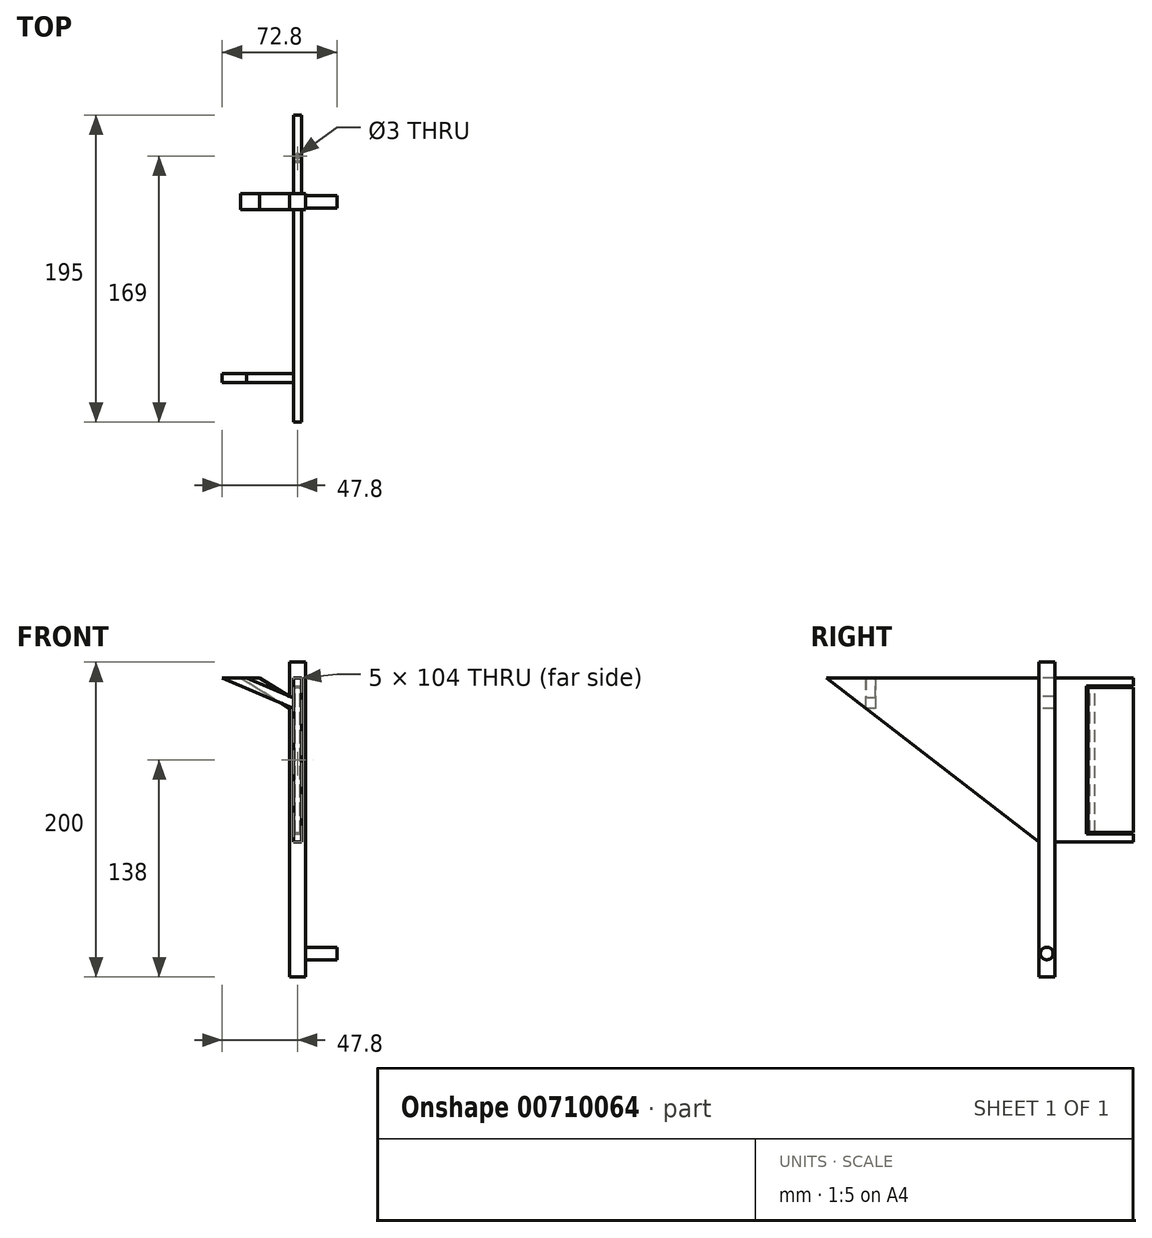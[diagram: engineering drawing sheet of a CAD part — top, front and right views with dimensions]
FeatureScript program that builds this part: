
annotation { "Feature Type Name" : "Feature", "Feature Type Description" : "" }
export const myFeature = defineFeature(function(context is Context, id is Id, definition is map)
    precondition{}
    {
        {
            var Q0;
            Q0=qCreatedBy(makeId("Front.planeOp"),FACE);
            var sketch = newSketch(context, id + "F0", { "sketchPlane" : qUnion([Q0])});
            skLineSegment(sketch, "E0.bottom", {"start": v(5, -100) * mm, "end": v(-5, -100) * mm});
            skLineSegment(sketch, "E0.top", {"start": v(5, 100) * mm, "end": v(-5, 100) * mm});
            skLineSegment(sketch, "E0.left", {"start": v(5, -100) * mm, "end": v(5, 100) * mm});
            skLineSegment(sketch, "E0.right", {"start": v(-5, -100) * mm, "end": v(-5, 100) * mm});
            skPoint(sketch, "E0.middle", {"position": v(0, 0) * mm});
            skSolve(sketch);
        }
        {
            var Q0;
            Q0 = qSketchRegion(id + "F0", true);
            extrude(context, id + "F1", {"entities" : qUnion([Q0]), "depth" : 10 * mm, "offsetDistance" : 25 * mm});
        }
        {
            var Q0;
            Q0=makeQuery(id+"F1.opExtrude","CAP_FACE",FACE,{"disambiguationData":[OSD([sQuery(id+"F0.wireOp",EDGE,"E0.bottom"),sQuery(id+"F0.wireOp",EDGE,"E0.top"),sQuery(id+"F0.wireOp",EDGE,"E0.left"),sQuery(id+"F0.wireOp",EDGE,"E0.right")])],"isStart":false});
            var sketch = newSketch(context, id + "F2", { "sketchPlane" : qUnion([Q0])});
            skLineSegment(sketch, "E1", {"start": v(0, 90) * mm, "end": v(2.5, 90) * mm});
            skLineSegment(sketch, "E2", {"start": v(2.5, 90) * mm, "end": v(2.5, -14) * mm});
            skLineSegment(sketch, "E3", {"start": v(2.5, -14) * mm, "end": v(0, -14) * mm});
            skLineSegment(sketch, "E4", {"start": v(0, -14) * mm, "end": v(-2.5, -14) * mm});
            skLineSegment(sketch, "E5", {"start": v(-2.5, -14) * mm, "end": v(-2.5, 90) * mm});
            skLineSegment(sketch, "E6", {"start": v(-2.5, 90) * mm, "end": v(0, 90) * mm});
            skSolve(sketch);
        }
        {
            var Q0;
            Q0 = qSketchRegion(id + "F2", true);
            extrude(context, id + "F3", {"entities" : qUnion([Q0]), "operationType" : NewBodyOperationType.ADD, "depth" : 135 * mm, "offsetDistance" : 25 * mm});
        }
        {
            var Q0;
            Q0=makeQuery(id+"F3.opExtrude","SWEPT_FACE",FACE,{"disambiguationData":[OSD([sQuery(id+"F2.wireOp",EDGE,"E2")])]});
            var sketch = newSketch(context, id + "F4", { "sketchPlane" : qUnion([Q0])});
            skLineSegment(sketch, "E7", {"start": v(-145, 90) * mm, "end": v(-145, -14) * mm});
            skLineSegment(sketch, "E8", {"start": v(-145, -14) * mm, "end": v(-10, -14) * mm});
            skLineSegment(sketch, "E9", {"start": v(-10, -14) * mm, "end": v(-145, 90) * mm});
            skSolve(sketch);
        }
        {
            var Q0;
            Q0 = qSketchRegion(id + "F4", true);
            extrude(context, id + "F5", {"entities" : qUnion([Q0]), "operationType" : NewBodyOperationType.REMOVE, "endBound" : BoundingType.THROUGH_ALL, "oppositeDirection" : true, "depth" : 25 * mm, "offsetDistance" : 25 * mm});
        }
        {
            var Q0;
            Q0=makeQuery(id+"F3.opExtrude","SWEPT_FACE",FACE,{"disambiguationData":[OSD([sQuery(id+"F2.wireOp",EDGE,"E5")])]});
            var sketch = newSketch(context, id + "F6", { "sketchPlane" : qUnion([Q0])});
            skLineSegment(sketch, "E10", {"start": v(10, 90) * mm, "end": v(114, 90) * mm});
            skLineSegment(sketch, "E11", {"start": v(114, 90) * mm, "end": v(120, 90) * mm});
            skLineSegment(sketch, "E12", {"start": v(114, 90) * mm, "end": v(114, 84) * mm});
            skLineSegment(sketch, "E13", {"start": v(114, 84) * mm, "end": v(120, 84) * mm});
            skLineSegment(sketch, "E14", {"start": v(120, 84) * mm, "end": v(120, 90) * mm});
            skLineSegment(sketch, "E15", {"start": v(10, 90) * mm, "end": v(10, 70.74) * mm});
            skLineSegment(sketch, "E16", {"start": v(10, 70.74) * mm, "end": v(114, 70.74) * mm});
            skLineSegment(sketch, "E17", {"start": v(114, 70.74) * mm, "end": v(120, 70.74) * mm});
            skLineSegment(sketch, "E18", {"start": v(114, 70.74) * mm, "end": v(114, 76.74) * mm});
            skLineSegment(sketch, "E19", {"start": v(114, 76.74) * mm, "end": v(120, 76.74) * mm});
            skLineSegment(sketch, "E20", {"start": v(120, 76.74) * mm, "end": v(120, 70.74) * mm});
            skLineSegment(sketch, "E21", {"start": v(120, 90) * mm, "end": v(120, 70.74) * mm});
            skLineSegment(sketch, "E22", {"start": v(114, 76.74) * mm, "end": v(114, 84) * mm});
            skLineSegment(sketch, "E23.bottom", {"start": v(120, 90) * mm, "end": v(114, 90) * mm});
            skLineSegment(sketch, "E23.top", {"start": v(120, 92) * mm, "end": v(114, 92) * mm});
            skLineSegment(sketch, "E23.left", {"start": v(120, 90) * mm, "end": v(120, 92) * mm});
            skLineSegment(sketch, "E23.right", {"start": v(114, 90) * mm, "end": v(114, 92) * mm});
            skSolve(sketch);
        }
        {
            var Q0;
            {var subQ0=sQuery(id+"F6.wireOp",EDGE,"E11");Q0=makeQuery(id+"F6.imprint","IMPRINT",FACE,{"disambiguationData":[TD([[makeQuery(id+"F6.imprint","IMPRINT",EDGE,{"derivedFrom":subQ0}),1.0]])]});}
            var Q1;
            {var subQ0=sQuery(id+"F6.wireOp",EDGE,"E17");Q1=makeQuery(id+"F6.imprint","IMPRINT",FACE,{"disambiguationData":[TD([[makeQuery(id+"F6.imprint","IMPRINT",EDGE,{"derivedFrom":subQ0}),1.0]])]});}
            var Q2;
            {var subQ0=sQuery(id+"F6.wireOp",EDGE,"E13");Q2=makeQuery(id+"F6.imprint","IMPRINT",FACE,{"disambiguationData":[TD([[makeQuery(id+"F6.imprint","IMPRINT",EDGE,{"derivedFrom":subQ0}),-1.0]])]});}
            var Q3;
            Q3=makeQuery(id+"F6.imprint","IMPRINT",FACE,{"disambiguationData":[TD([[makeQuery(id+"F6.imprint","IMPRINT",EDGE,{"derivedFrom":sQuery(id+"F6.wireOp",EDGE,"E12")}),1.0]])]});
            var Q4;
            Q4=makeQuery(id+"F6.imprint","IMPRINT",FACE,{"disambiguationData":[TD([[makeQuery(id+"F6.imprint","IMPRINT",EDGE,{"derivedFrom":sQuery(id+"F6.wireOp",EDGE,"E23.bottom")}),-1.0]])]});
            extrude(context, id + "F7", {"entities" : qUnion([Q0, Q1, Q2, Q3, Q4]), "operationType" : NewBodyOperationType.ADD, "depth" : 50 * mm, "offsetDistance" : 25 * mm});
        }
        {
            var Q0;
            Q0=makeQuery(id+"F7.opExtrude","SWEPT_FACE",FACE,{"disambiguationData":[OSD([sQuery(id+"F6.wireOp",EDGE,"E21")])]});
            var sketch = newSketch(context, id + "F8", { "sketchPlane" : qUnion([Q0])});
            skLineSegment(sketch, "E24", {"start": v(-2.5, 70.74) * mm, "end": v(-52.5, 92) * mm});
            skLineSegment(sketch, "E25", {"start": v(-37.17, 92) * mm, "end": v(-2.5, 77.26) * mm});
            skSolve(sketch);
        }
        {
            var Q0;
            Q0=makeQuery(id+"F8.imprint","IMPRINT",FACE,{"disambiguationData":[TD([[makeQuery(id+"F8.imprint","IMPRINT",EDGE,{"derivedFrom":sQuery(id+"F8.wireOp",EDGE,"qwdXAB4e-E5ou-LqlY-9mqs-tjVmSu6iFq8c")}),1.0]])]});
            var Q1;
            {var subQ0=sQuery(id+"F8.wireOp",EDGE,"3mmgTVSa-EUJ8-fqU7-aLnw-NF2mhHhyj2O0");Q1=makeQuery(id+"F8.imprint","IMPRINT",FACE,{"disambiguationData":[TD([[makeQuery(id+"F8.imprint","IMPRINT",EDGE,{"derivedFrom":subQ0}),1.0]])]});}
            var Q2;
            {var subQ0=sQuery(id+"F8.wireOp",EDGE,"P0UW7KZ7-9kCL-0TL6-S78o-fbrZpAh6waou");Q2=makeQuery(id+"F8.imprint","IMPRINT",FACE,{"disambiguationData":[TD([[makeQuery(id+"F8.imprint","IMPRINT",EDGE,{"derivedFrom":subQ0}),1.0]])]});}
            var Q3;
            Q3=makeQuery(id+"F8.imprint","IMPRINT",FACE,{"disambiguationData":[TD([[makeQuery(id+"F8.imprint","IMPRINT",EDGE,{"derivedFrom":sQuery(id+"F8.wireOp",EDGE,"kPvC1WPp-rgsQ-izWo-Zl4w-EBVaQ9JV2pb9")}),1.0]])]});
            var Q4;
            Q4=makeQuery(id+"F8.imprint","IMPRINT",FACE,{"disambiguationData":[TD([[makeQuery(id+"F8.imprint","IMPRINT",EDGE,{"derivedFrom":sQuery(id+"F8.wireOp",EDGE,"E24")}),1.0]])]});
            var Q5;
            {var subQ0=sQuery(id+"F8.wireOp",EDGE,"E25");Q5=makeQuery(id+"F8.imprint","IMPRINT",FACE,{"disambiguationData":[TD([[makeQuery(id+"F8.imprint","IMPRINT",EDGE,{"derivedFrom":subQ0}),1.0]])]});}
            var Q6;
            Q6=makeQuery(id+"F7.opExtrude","SWEPT_FACE",FACE,{"disambiguationData":[OSD([sQuery(id+"F6.wireOp",EDGE,"E12"),sQuery(id+"F6.wireOp",EDGE,"E18"),sQuery(id+"F6.wireOp",EDGE,"E22")])]});
            extrude(context, id + "F9", {"entities" : qUnion([Q0, Q1, Q2, Q3, Q4, Q5]), "operationType" : NewBodyOperationType.REMOVE, "endBound" : BoundingType.UP_TO_SURFACE, "oppositeDirection" : true, "depth" : 25 * mm, "endBoundEntityFace" : qUnion([Q6]), "offsetDistance" : 25 * mm});
        }
        {
            var Q0;
            Q0=makeQuery(id+"F1.opExtrude","SWEPT_FACE",FACE,{"disambiguationData":[OSD([sQuery(id+"F0.wireOp",EDGE,"E0.right")])]});
            var sketch = newSketch(context, id + "F10", { "sketchPlane" : qUnion([Q0])});
            skLineSegment(sketch, "E26", {"start": v(5, 100) * mm, "end": v(5, 45.97) * mm});
            skLineSegment(sketch, "E27", {"start": v(5, 100) * mm, "end": v(5, 90) * mm});
            skLineSegment(sketch, "E28", {"start": v(5, 90) * mm, "end": v(5, 70.75) * mm});
            skLineSegment(sketch, "E29", {"start": v(5, 70.75) * mm, "end": v(10, 70.75) * mm});
            skLineSegment(sketch, "E30", {"start": v(10, 70.75) * mm, "end": v(10, 80.75) * mm});
            skLineSegment(sketch, "E31", {"start": v(10, 80.75) * mm, "end": v(0, 80.75) * mm});
            skLineSegment(sketch, "E32", {"start": v(0, 80.75) * mm, "end": v(0, 70.75) * mm});
            skLineSegment(sketch, "E33", {"start": v(0, 70.75) * mm, "end": v(5, 70.75) * mm});
            skLineSegment(sketch, "E34", {"start": v(10, 80.75) * mm, "end": v(10, 90) * mm});
            skLineSegment(sketch, "E35", {"start": v(10, 90) * mm, "end": v(0, 90) * mm});
            skLineSegment(sketch, "E36", {"start": v(0, 90) * mm, "end": v(0, 80.75) * mm});
            skSolve(sketch);
        }
        {
            var Q0;
            {var subQ0=sQuery(id+"F10.wireOp",EDGE,"E29");Q0=makeQuery(id+"F10.imprint","IMPRINT",FACE,{"disambiguationData":[TD([[makeQuery(id+"F10.imprint","IMPRINT",EDGE,{"derivedFrom":subQ0}),1.0]])]});}
            var Q1;
            {var subQ4=sQuery(id+"F10.wireOp",EDGE,"E32");Q1=makeQuery(id+"F10.imprint","IMPRINT",FACE,{"disambiguationData":[TD([[makeQuery(id+"F10.imprint","IMPRINT",EDGE,{"derivedFrom":subQ4}),-1.0]])]});}
            var Q2;
            {var subQ5=sQuery(id+"F10.wireOp",EDGE,"E36");Q2=makeQuery(id+"F10.imprint","IMPRINT",FACE,{"disambiguationData":[TD([[makeQuery(id+"F10.imprint","IMPRINT",EDGE,{"derivedFrom":subQ5}),-1.0]])]});}
            var Q3;
            {var subQ5=sQuery(id+"F10.wireOp",EDGE,"E34");Q3=makeQuery(id+"F10.imprint","IMPRINT",FACE,{"disambiguationData":[TD([[makeQuery(id+"F10.imprint","IMPRINT",EDGE,{"derivedFrom":subQ5}),1.0]])]});}
            var Q4;
            {var subQ0=sQuery(id+"F10.wireOp",EDGE,"E27");Q4=makeQuery(id+"F10.imprint","IMPRINT",FACE,{"disambiguationData":[TD([[makeQuery(id+"F10.imprint","IMPRINT",EDGE,{"derivedFrom":subQ0}),1.0]])]});}
            var Q5;
            {var subQ0=sQuery(id+"F10.wireOp",EDGE,"E27");Q5=makeQuery(id+"F10.imprint","IMPRINT",FACE,{"disambiguationData":[TD([[makeQuery(id+"F10.imprint","IMPRINT",EDGE,{"derivedFrom":subQ0}),-1.0]])]});}
            extrude(context, id + "F11", {"entities" : qUnion([Q0, Q1, Q2, Q3, Q4, Q5]), "operationType" : NewBodyOperationType.ADD, "depth" : 47.5 * mm, "offsetDistance" : 25 * mm});
        }
        {
            var Q0;
            Q0=makeQuery(id+"F11.boolean.opBoolean","MERGE",FACE,{"derivedFrom":[makeQuery(id+"F1.opExtrude","CAP_FACE",FACE,{"disambiguationData":[OSD([sQuery(id+"F0.wireOp",EDGE,"E0.bottom"),sQuery(id+"F0.wireOp",EDGE,"E0.top"),sQuery(id+"F0.wireOp",EDGE,"E0.left"),sQuery(id+"F0.wireOp",EDGE,"E0.right")])],"isStart":false}),makeQuery(id+"F11.opExtrude","SWEPT_FACE",FACE,{"disambiguationData":[OSD([sQuery(id+"F10.wireOp",EDGE,"E30"),sQuery(id+"F10.wireOp",EDGE,"E34")])]})]});
            var sketch = newSketch(context, id + "F12", { "sketchPlane" : qUnion([Q0])});
            skLineSegment(sketch, "E37", {"start": v(-52.5, 100) * mm, "end": v(-5, 70.75) * mm});
            skLineSegment(sketch, "E38", {"start": v(-5, 70.75) * mm, "end": v(-2.5, 70.75) * mm});
            skLineSegment(sketch, "E39", {"start": v(-5, 70.75) * mm, "end": v(-5, 100) * mm});
            skLineSegment(sketch, "E40", {"start": v(-40.23, 100) * mm, "end": v(-5, 78.3) * mm});
            skSolve(sketch);
        }
        {
            var Q0;
            {var subQ6=sQuery(id+"F12.wireOp",EDGE,"LR92XTVL-ZGK5-bEUs-Z0Es-jbydp57ibUwi");Q0=makeQuery(id+"F12.imprint","IMPRINT",FACE,{"disambiguationData":[TD([[makeQuery(id+"F12.imprint","IMPRINT",EDGE,{"derivedFrom":subQ6}),-1.0]])]});}
            var Q1;
            Q1=makeQuery(id+"F12.imprint","IMPRINT",FACE,{"disambiguationData":[TD([[makeQuery(id+"F12.imprint","IMPRINT",EDGE,{"derivedFrom":sQuery(id+"F12.wireOp",EDGE,"E37")}),-1.0]])]});
            var Q2;
            {var subQ5=sQuery(id+"F12.wireOp",EDGE,"E40");Q2=makeQuery(id+"F12.imprint","IMPRINT",FACE,{"disambiguationData":[TD([[makeQuery(id+"F12.imprint","IMPRINT",EDGE,{"derivedFrom":subQ5}),1.0]])]});}
            var Q3;
            Q3=makeQuery(id+"F11.boolean.opBoolean","MERGE",FACE,{"derivedFrom":[makeQuery(id+"F1.opExtrude","CAP_FACE",FACE,{"disambiguationData":[OSD([sQuery(id+"F0.wireOp",EDGE,"E0.bottom"),sQuery(id+"F0.wireOp",EDGE,"E0.top"),sQuery(id+"F0.wireOp",EDGE,"E0.left"),sQuery(id+"F0.wireOp",EDGE,"E0.right")])],"isStart":true}),makeQuery(id+"F11.opExtrude","SWEPT_FACE",FACE,{"disambiguationData":[OSD([sQuery(id+"F10.wireOp",EDGE,"E32"),sQuery(id+"F10.wireOp",EDGE,"E36")])]})]});
            extrude(context, id + "F13", {"entities" : qUnion([Q0, Q1, Q2]), "operationType" : NewBodyOperationType.REMOVE, "endBound" : BoundingType.UP_TO_SURFACE, "oppositeDirection" : true, "depth" : 25 * mm, "endBoundEntityFace" : qUnion([Q3]), "offsetDistance" : 25 * mm});
        }
        {
            var Q0;
            Q0=makeQuery(id+"F1.opExtrude","SWEPT_FACE",FACE,{"disambiguationData":[OSD([sQuery(id+"F0.wireOp",EDGE,"E0.left")])]});
            var sketch = newSketch(context, id + "F14", { "sketchPlane" : qUnion([Q0])});
            skLineSegment(sketch, "E41", {"start": v(-5, -100) * mm, "end": v(-5, -85) * mm});
            skCircle(sketch, "E42", {"center": v(-5, -85) * mm, "radius": 4 * mm});
            skSolve(sketch);
        }
        {
            var Q0;
            Q0=makeQuery(id+"F14.imprint","IMPRINT",FACE,{"disambiguationData":[TD([[makeQuery(id+"F14.imprint","IMPRINT",EDGE,{"derivedFrom":sQuery(id+"F14.wireOp",EDGE,"E42")}),1.0]])]});
            extrude(context, id + "F15", {"entities" : qUnion([Q0]), "operationType" : NewBodyOperationType.ADD, "depth" : 20 * mm, "offsetDistance" : 25 * mm});
        }
        {
            var Q0;
            Q0=makeQuery(id+"F11.boolean.opBoolean","MERGE",FACE,{"derivedFrom":[makeQuery(id+"F1.opExtrude","CAP_FACE",FACE,{"disambiguationData":[OSD([sQuery(id+"F0.wireOp",EDGE,"E0.bottom"),sQuery(id+"F0.wireOp",EDGE,"E0.top"),sQuery(id+"F0.wireOp",EDGE,"E0.left"),sQuery(id+"F0.wireOp",EDGE,"E0.right")])],"isStart":true}),makeQuery(id+"F11.opExtrude","SWEPT_FACE",FACE,{"disambiguationData":[OSD([sQuery(id+"F10.wireOp",EDGE,"E32"),sQuery(id+"F10.wireOp",EDGE,"E36")])]})]});
            var sketch = newSketch(context, id + "F16", { "sketchPlane" : qUnion([Q0])});
            skLineSegment(sketch, "E43", {"start": v(0, 90) * mm, "end": v(2.5, 90) * mm});
            skLineSegment(sketch, "E44", {"start": v(0, 90) * mm, "end": v(-2.5, 90) * mm});
            skLineSegment(sketch, "E45.bottom", {"start": v(-2.5, 90) * mm, "end": v(2.5, 90) * mm});
            skLineSegment(sketch, "E45.top", {"start": v(-2.5, -14) * mm, "end": v(2.5, -14) * mm});
            skLineSegment(sketch, "E45.left", {"start": v(-2.5, 90) * mm, "end": v(-2.5, -14) * mm});
            skLineSegment(sketch, "E45.right", {"start": v(2.5, 90) * mm, "end": v(2.5, -14) * mm});
            skPoint(sketch, "E46.start.orphan", {"position": v(0, 100) * mm});
            skSolve(sketch);
        }
        {
            var Q0;
            Q0 = qSketchRegion(id + "F16", true);
            extrude(context, id + "F17", {"entities" : qUnion([Q0]), "operationType" : NewBodyOperationType.ADD, "depth" : 50 * mm, "offsetDistance" : 25 * mm});
        }
        {
            var Q0;
            Q0=makeQuery(id+"F17.opExtrude","SWEPT_FACE",FACE,{"disambiguationData":[OSD([sQuery(id+"F16.wireOp",EDGE,"E45.left")])]});
            var sketch = newSketch(context, id + "F18", { "sketchPlane" : qUnion([Q0])});
            skLineSegment(sketch, "E47", {"start": v(50, 85) * mm, "end": v(20, 85) * mm});
            skLineSegment(sketch, "E48", {"start": v(20, 85) * mm, "end": v(20, -9) * mm});
            skLineSegment(sketch, "E49", {"start": v(20, -9) * mm, "end": v(50, -9) * mm});
            skLineSegment(sketch, "E50", {"start": v(50, 85) * mm, "end": v(50, 84) * mm});
            skLineSegment(sketch, "E51", {"start": v(50, 84) * mm, "end": v(21, 84) * mm});
            skLineSegment(sketch, "E52", {"start": v(21, 84) * mm, "end": v(21, -8) * mm});
            skLineSegment(sketch, "E53", {"start": v(21, -8) * mm, "end": v(50, -8) * mm});
            skSolve(sketch);
        }
        {
            var Q0;
            Q0=makeQuery(id+"F18.imprint","IMPRINT",FACE,{"disambiguationData":[TD([[makeQuery(id+"F18.imprint","IMPRINT",EDGE,{"derivedFrom":sQuery(id+"F18.wireOp",EDGE,"E47")}),1.0]])]});
            var Q1;
            Q1=makeQuery(id+"F17.opExtrude","SWEPT_FACE",FACE,{"disambiguationData":[OSD([sQuery(id+"F16.wireOp",EDGE,"E45.right")])]});
            extrude(context, id + "F19", {"entities" : qUnion([Q0]), "operationType" : NewBodyOperationType.REMOVE, "endBound" : BoundingType.UP_TO_SURFACE, "oppositeDirection" : true, "depth" : 25 * mm, "endBoundEntityFace" : qUnion([Q1]), "offsetDistance" : 25 * mm});
        }
        {
            var Q0;
            Q0=makeQuery(id+"F19.boolean.opBoolean","COPY",FACE,{"derivedFrom":makeQuery(id+"F19.opExtrude","SWEPT_FACE",FACE,{"disambiguationData":[OSD([sQuery(id+"F18.wireOp",EDGE,"E51")])]})});
            var sketch = newSketch(context, id + "F20", { "sketchPlane" : qUnion([Q0])});
            skLineSegment(sketch, "E54", {"start": v(0, 21) * mm, "end": v(0, 24) * mm});
            skCircle(sketch, "E55", {"center": v(0, 24) * mm, "radius": 1.5 * mm});
            skSolve(sketch);
        }
        {
            var Q0;
            Q0 = qSketchRegion(id + "F20", true);
            var Q1;
            Q1=makeQuery(id+"F19.boolean.opBoolean","COPY",FACE,{"derivedFrom":makeQuery(id+"F19.opExtrude","SWEPT_FACE",FACE,{"disambiguationData":[OSD([sQuery(id+"F18.wireOp",EDGE,"E53")])]})});
            extrude(context, id + "F21", {"entities" : qUnion([Q0]), "operationType" : NewBodyOperationType.REMOVE, "endBound" : BoundingType.UP_TO_SURFACE, "oppositeDirection" : true, "depth" : 25 * mm, "endBoundEntityFace" : qUnion([Q1]), "offsetDistance" : 25 * mm});
        }
        {
            var Q0;
            Q0=makeQuery(id+"F19.boolean.opBoolean","COPY",FACE,{"derivedFrom":makeQuery(id+"F19.opExtrude","SWEPT_FACE",FACE,{"disambiguationData":[OSD([sQuery(id+"F18.wireOp",EDGE,"E47")])]})});
            var sketch = newSketch(context, id + "F22", { "sketchPlane" : qUnion([Q0])});
            skLineSegment(sketch, "E56", {"start": v(0, -20) * mm, "end": v(0, -24) * mm});
            skCircle(sketch, "E57", {"center": v(0, -24) * mm, "radius": 1.5 * mm});
            skLineSegment(sketch, "E58", {"start": v(0, -50) * mm, "end": v(0, -20) * mm});
            skSolve(sketch);
        }
        {
            var Q0;
            Q0 = qSketchRegion(id + "F22", true);
            var Q1;
            Q1=makeQuery(id+"F19.boolean.opBoolean","COPY",FACE,{"derivedFrom":makeQuery(id+"F19.opExtrude","SWEPT_FACE",FACE,{"disambiguationData":[OSD([sQuery(id+"F18.wireOp",EDGE,"E49")])]})});
            extrude(context, id + "F23", {"entities" : qUnion([Q0]), "endBound" : BoundingType.UP_TO_SURFACE, "depth" : 25 * mm, "endBoundEntityFace" : qUnion([Q1]), "offsetDistance" : 25 * mm});
        }
    });
